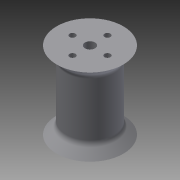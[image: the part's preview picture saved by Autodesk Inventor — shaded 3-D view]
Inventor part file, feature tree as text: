
AUTODESK INVENTOR PART (.ipt)
format: ipt  version: 2015 (Build 190159000, 159)  size: 119,296 bytes
history: native  units: in
note: dims shown in document units (in); Inventor stores cm internally (conversion verified against a paired STEP export)
features: sketch x2, revolve x1, extrude x1
ambient origin geometry x8: Origin, YZ Plane, XZ Plane, XY Plane, X Axis, Y Axis, Z Axis, Center Point
bodies: Solid1 (feature_tree)
feature tree (4):
  revolve  "Revolution1"  Angle=45.0deg
  extrude  "Extrusion1"  TaperAngle=90.0deg  [1 undecoded]
  sketch  "Sketch2"  dims[d1=0.6in d2=45.0deg]
  sketch  "Sketch3"  dims[d3=1.394in d4=90.0deg d5=0.125in d6=0.4331in d7=1.0in d8=0.0in d9=0.1065in d10=0.183in]
note: 1 required parameter value undecoded (feature->parameter linkage not recoverable at this tier; creation-order binding heuristic only, values carry confidence <= 0.55)
